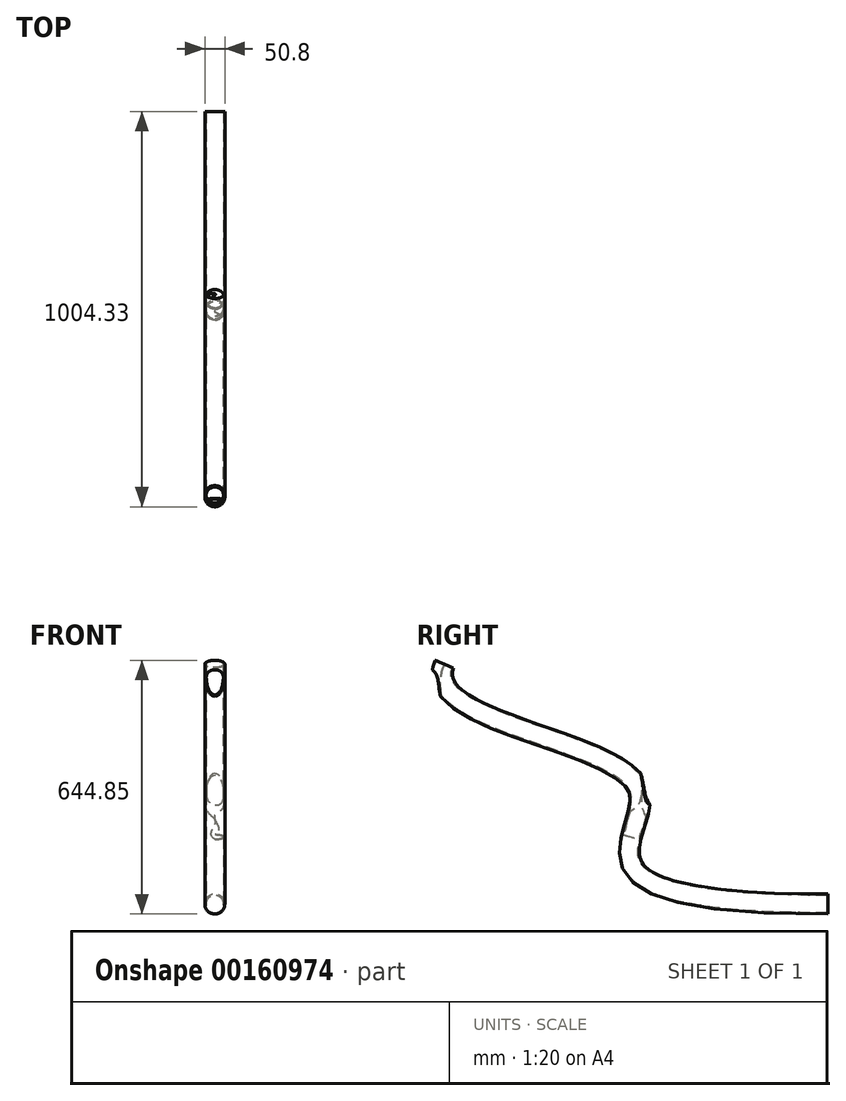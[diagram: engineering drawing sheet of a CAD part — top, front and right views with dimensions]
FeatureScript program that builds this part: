
annotation { "Feature Type Name" : "Feature", "Feature Type Description" : "" }
export const myFeature = defineFeature(function(context is Context, id is Id, definition is map)
    precondition{}
    {
        {
            var Q0;
            Q0=qCreatedBy(makeId("Front.planeOp"),FACE);
            var sketch = newSketch(context, id + "F0", { "sketchPlane" : qUnion([Q0])});
            skCircle(sketch, "E0", {"center": v(-0.52, -3.5) * mm, "radius": 25.4 * mm});
            skCircle(sketch, "E1.0", {"center": v(-0.52, -3.5) * mm, "radius": 22.23 * mm});
            skSolve(sketch);
        }
        {
            var Q0;
            Q0=qCreatedBy(makeId("Right.planeOp"),FACE);
            var sketch = newSketch(context, id + "F1", { "sketchPlane" : qUnion([Q0])});
            skFitSpline(sketch, "E2", {"points": [v(0, -3.5) * mm, v(-487.09, 301.3) * mm, v(-974.17, 606.1) * mm], "startDerivative": vector(-4541.65, 0) * mm, "endDerivative": vector(372.1, 883.87) * mm});
            skLineSegment(sketch, "E3", {"start": v(-487.09, 301.3) * mm, "end": v(0, 301.3) * mm, "construction": true});
            skLineSegment(sketch, "E4", {"start": v(0, 301.3) * mm, "end": v(0, -3.5) * mm, "construction": true});
            skLineSegment(sketch, "E5", {"start": v(-487.09, 301.3) * mm, "end": v(-974.17, 301.3) * mm, "construction": true});
            skLineSegment(sketch, "E6", {"start": v(-974.17, 301.3) * mm, "end": v(-974.17, 606.1) * mm, "construction": true});
            skPoint(sketch, "E7", {"position": v(-499.04, 166.81) * mm});
            skPoint(sketch, "E8", {"position": v(-488.05, 204.68) * mm});
            skLineSegment(sketch, "E9", {"start": v(-499.04, 166.81) * mm, "end": v(-488.05, 204.68) * mm, "construction": true});
            skSolve(sketch);
        }
        {
            var Q0;
            Q0=makeQuery(id+"F0.imprint","IMPRINT",FACE,{"disambiguationData":[TD([[makeQuery(id+"F0.imprint","IMPRINT",EDGE,{"derivedFrom":sQuery(id+"F0.wireOp",EDGE,"E0")}),1.0]])]});
            var Q1;
            Q1=sQuery(id+"F1.wireOp",EDGE,"E2");
            sweep(context, id + "F2", {"profiles" : qUnion([Q0]), "path" : qUnion([Q1])});
        }
        {
            var Q0;
            Q0=makeQuery(id+"F2.opSweep","CAP_FACE",FACE,{"disambiguationData":[OSD([sQuery(id+"F0.wireOp",EDGE,"E0"),sQuery(id+"F0.wireOp",EDGE,"E1.0"),sQuery(id+"F1.wireOp",VERTEX,"E2.end")])],"isStart":false});
            var sketch = newSketch(context, id + "F3", { "sketchPlane" : qUnion([Q0])});
            skCircle(sketch, "E10.0", {"center": v(-0.52, -1133.03) * mm, "radius": 22.23 * mm});
            skSolve(sketch);
        }
        {
            var Q0;
            Q0=makeQuery(id+"F3.imprint","IMPRINT",FACE,{"disambiguationData":[TD([[makeQuery(id+"F3.imprint","IMPRINT",EDGE,{"derivedFrom":sQuery(id+"F3.wireOp",EDGE,"E10.0")}),1.0]])]});
            extrude(context, id + "F4", {"entities" : qUnion([Q0]), "operationType" : NewBodyOperationType.REMOVE, "oppositeDirection" : true, "depth" : 104.77 * mm});
        }
        {
            var Q0;
            Q0=qCreatedBy(makeId("Right.planeOp"),FACE);
            var sketch = newSketch(context, id + "F5", { "sketchPlane" : qUnion([Q0])});
            skLineSegment(sketch, "E11", {"start": v(-499.04, 166.81) * mm, "end": v(-430.77, 401.88) * mm, "construction": true});
            skLineSegment(sketch, "E12", {"start": v(-430.77, 401.88) * mm, "end": v(-409.43, 395.68) * mm});
            skLineSegment(sketch, "E13", {"start": v(-409.43, 395.68) * mm, "end": v(-477.7, 160.61) * mm});
            skLineSegment(sketch, "E14", {"start": v(-477.7, 160.61) * mm, "end": v(-499.04, 166.81) * mm});
            skLineSegment(sketch, "E15", {"start": v(-430.77, 401.88) * mm, "end": v(-499.04, 166.81) * mm});
            skSolve(sketch);
        }
        {
            var Q0;
            Q0=makeQuery(id+"F5.imprint","IMPRINT",FACE,{"disambiguationData":[TD([[makeQuery(id+"F5.imprint","IMPRINT",EDGE,{"derivedFrom":sQuery(id+"F5.wireOp",EDGE,"E12")}),-1.0]])]});
            var Q1;
            Q1=sQuery(id+"F5.wireOp",EDGE,"E15");
            revolve(context, id + "F6", {"operationType" : NewBodyOperationType.REMOVE, "entities" : qUnion([Q0]), "axis" : qUnion([Q1]), "revolveType" : RevolveType.FULL, "oppositeDirection" : true});
        }
    });
